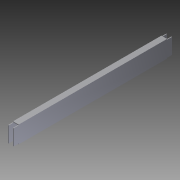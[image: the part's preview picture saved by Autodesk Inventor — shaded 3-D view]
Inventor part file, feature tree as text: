
AUTODESK INVENTOR PART (.ipt)
format: ipt  version: 2012 (Build 160160000, 160)  size: 105,984 bytes
history: native  units: in
note: dims shown in document units (in); Inventor stores cm internally (conversion verified against a paired STEP export)
features: extrude x3, sketch x3
ambient origin geometry x8: Origin, YZ Plane, XZ Plane, XY Plane, X Axis, Y Axis, Z Axis, Center Point
bodies: Solid1 (feature_tree)
feature tree (6):
  extrude  "Extrusion1"  Depth=3.0in
  extrude  "Extrusion2"  Depth=0.125in
  extrude  "Extrusion3"  Depth=0.125in
  sketch  "Sketch1"  dims[d0=1.0in d1=3.0in]
  sketch  "Sketch2"  dims[d2=0.125in d3=0.125in]
  sketch  "Sketch3"  dims[d4=0.125in d5=0.125in d6=27.75in d7=0.0in d8=0.875in d9=0.875in d10=0.125in d11=0.0in d12=0.875in d13=0.875in d14=0.125in d15=0.0in]
